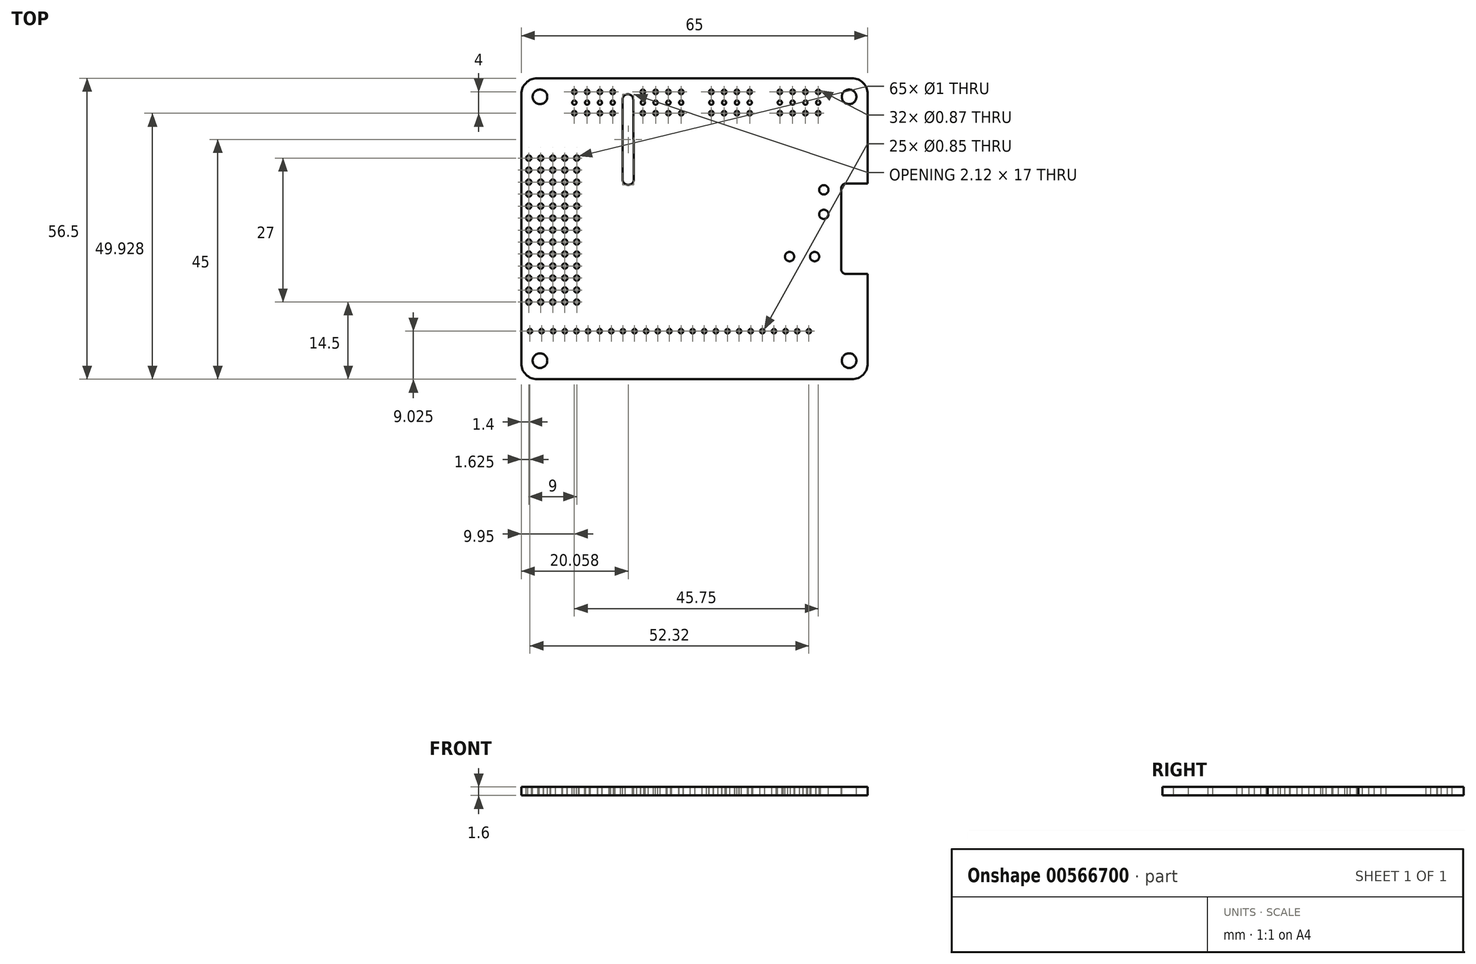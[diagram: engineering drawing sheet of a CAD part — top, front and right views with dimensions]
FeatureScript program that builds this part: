
annotation { "Feature Type Name" : "Feature", "Feature Type Description" : "" }
export const myFeature = defineFeature(function(context is Context, id is Id, definition is map)
    precondition{}
    {
        {
            var Q0;
            Q0=qCreatedBy(makeId("Top.planeOp"),FACE);
            var sketch = newSketch(context, id + "F0", { "sketchPlane" : qUnion([Q0])});
            skLineSegment(sketch, "E0.bottom", {"start": v(32.5, 28.25) * mm, "end": v(-32.5, 28.25) * mm});
            skLineSegment(sketch, "E0.top", {"start": v(32.5, -28.25) * mm, "end": v(-32.5, -28.25) * mm});
            skLineSegment(sketch, "E0.left", {"start": v(32.5, 28.25) * mm, "end": v(32.5, -28.25) * mm});
            skLineSegment(sketch, "E0.right", {"start": v(-32.5, 28.25) * mm, "end": v(-32.5, -28.25) * mm});
            skPoint(sketch, "E0.middle", {"position": v(0, 0) * mm});
            skSolve(sketch);
        }
        {
            var Q0;
            Q0=makeQuery(id+"F0.imprint","IMPRINT",FACE,{"disambiguationData":[TD([[makeQuery(id+"F0.imprint","IMPRINT",EDGE,{"derivedFrom":sQuery(id+"F0.wireOp",EDGE,"E0.bottom")}),1.0]])]});
            extrude(context, id + "F1", {"entities" : qUnion([Q0]), "depth" : 1.6 * mm, "offsetDistance" : 25 * mm});
        }
        {
            var Q0;
            Q0=makeQuery(id+"F1.opExtrude","SWEPT_EDGE",EDGE,{"disambiguationData":[OSD([sQuery(id+"F0.wireOp",EDGE,"E0.top"),sQuery(id+"F0.wireOp",EDGE,"E0.right")])]});
            var Q1;
            Q1=makeQuery(id+"F1.opExtrude","SWEPT_EDGE",EDGE,{"disambiguationData":[OSD([sQuery(id+"F0.wireOp",EDGE,"E0.top"),sQuery(id+"F0.wireOp",EDGE,"E0.left")])]});
            var Q2;
            Q2=makeQuery(id+"F1.opExtrude","SWEPT_EDGE",EDGE,{"disambiguationData":[OSD([sQuery(id+"F0.wireOp",EDGE,"E0.bottom"),sQuery(id+"F0.wireOp",EDGE,"E0.left")])]});
            var Q3;
            Q3=makeQuery(id+"F1.opExtrude","SWEPT_EDGE",EDGE,{"disambiguationData":[OSD([sQuery(id+"F0.wireOp",EDGE,"E0.bottom"),sQuery(id+"F0.wireOp",EDGE,"E0.right")])]});
            fillet(context, id + "F2", {"entities" : qUnion([Q0, Q1, Q2, Q3]), "radius" : 3 * mm, "tangentPropagation" : true, "allowEdgeOverflow" : false});
        }
        {
            var Q0;
            Q0=makeQuery(id+"F1.opExtrude","CAP_FACE",FACE,{"disambiguationData":[OSD([sQuery(id+"F0.wireOp",EDGE,"E0.bottom"),sQuery(id+"F0.wireOp",EDGE,"E0.top"),sQuery(id+"F0.wireOp",EDGE,"E0.left"),sQuery(id+"F0.wireOp",EDGE,"E0.right")])],"isStart":false});
            var sketch = newSketch(context, id + "F3", { "sketchPlane" : qUnion([Q0])});
            skLineSegment(sketch, "E1.bottom", {"start": v(32.5, -8.5) * mm, "end": v(27.5, -8.5) * mm});
            skLineSegment(sketch, "E1.top", {"start": v(32.5, 8.5) * mm, "end": v(27.5, 8.5) * mm});
            skLineSegment(sketch, "E1.left", {"start": v(32.5, -8.5) * mm, "end": v(32.5, 8.5) * mm});
            skLineSegment(sketch, "E1.right", {"start": v(27.5, -8.5) * mm, "end": v(27.5, 8.5) * mm});
            skLineSegment(sketch, "E2", {"start": v(0, 0) * mm, "end": v(36, 0) * mm, "construction": true});
            skSolve(sketch);
        }
        {
            var Q0;
            Q0=makeQuery(id+"F3.imprint","IMPRINT",FACE,{"disambiguationData":[TD([[makeQuery(id+"F3.imprint","IMPRINT",EDGE,{"derivedFrom":sQuery(id+"F3.wireOp",EDGE,"E1.bottom")}),-1.0]])]});
            extrude(context, id + "F4", {"entities" : qUnion([Q0]), "operationType" : NewBodyOperationType.REMOVE, "endBound" : BoundingType.THROUGH_ALL, "oppositeDirection" : true, "depth" : 25 * mm, "offsetDistance" : 25 * mm});
        }
        {
            var Q0;
            Q0=makeQuery(id+"F4.boolean.opBoolean","COPY",EDGE,{"derivedFrom":makeQuery(id+"F4.opExtrude","SWEPT_EDGE",EDGE,{"disambiguationData":[OSD([sQuery(id+"F3.wireOp",EDGE,"E1.bottom"),sQuery(id+"F3.wireOp",EDGE,"E1.right")])]})});
            var Q1;
            Q1=makeQuery(id+"F4.boolean.opBoolean","COPY",EDGE,{"derivedFrom":makeQuery(id+"F4.opExtrude","SWEPT_EDGE",EDGE,{"disambiguationData":[OSD([sQuery(id+"F3.wireOp",EDGE,"E1.top"),sQuery(id+"F3.wireOp",EDGE,"E1.right")])]})});
            fillet(context, id + "F5", {"entities" : qUnion([Q0, Q1]), "radius" : 1 * mm, "tangentPropagation" : true, "allowEdgeOverflow" : false});
        }
        {
            var Q0;
            Q0=makeQuery(id+"F1.opExtrude","CAP_FACE",FACE,{"disambiguationData":[OSD([sQuery(id+"F0.wireOp",EDGE,"E0.bottom"),sQuery(id+"F0.wireOp",EDGE,"E0.top"),sQuery(id+"F0.wireOp",EDGE,"E0.left"),sQuery(id+"F0.wireOp",EDGE,"E0.right")])],"isStart":false});
            var sketch = newSketch(context, id + "F6", { "sketchPlane" : qUnion([Q0])});
            skCircle(sketch, "E3", {"center": v(-29, -24.75) * mm, "radius": 1.38 * mm});
            skCircle(sketch, "E4.MirrorC", {"center": v(29, -24.75) * mm, "radius": 1.38 * mm});
            skCircle(sketch, "E5.MirrorC", {"center": v(-29, 24.75) * mm, "radius": 1.38 * mm});
            skCircle(sketch, "E6.MirrorC", {"center": v(29, 24.75) * mm, "radius": 1.38 * mm});
            skSolve(sketch);
        }
        {
            var Q0;
            Q0 = qSketchRegion(id + "F6", true);
            extrude(context, id + "F7", {"entities" : qUnion([Q0]), "operationType" : NewBodyOperationType.REMOVE, "endBound" : BoundingType.THROUGH_ALL, "oppositeDirection" : true, "depth" : 25 * mm, "offsetDistance" : 25 * mm});
        }
        {
            var Q0;
            Q0=makeQuery(id+"F1.opExtrude","CAP_FACE",FACE,{"disambiguationData":[OSD([sQuery(id+"F0.wireOp",EDGE,"E0.bottom"),sQuery(id+"F0.wireOp",EDGE,"E0.top"),sQuery(id+"F0.wireOp",EDGE,"E0.left"),sQuery(id+"F0.wireOp",EDGE,"E0.right")])],"isStart":false});
            var sketch = newSketch(context, id + "F8", { "sketchPlane" : qUnion([Q0])});
            skCircle(sketch, "E7", {"center": v(-31.1, -13.75) * mm, "radius": 0.5 * mm});
            skCircle(sketch, "E8.0.1.0", {"center": v(-31.1, -11.5) * mm, "radius": 0.5 * mm});
            skCircle(sketch, "E8.0.2.0", {"center": v(-31.1, -9.25) * mm, "radius": 0.5 * mm});
            skCircle(sketch, "E8.0.3.0", {"center": v(-31.1, -7) * mm, "radius": 0.5 * mm});
            skCircle(sketch, "E8.0.4.0", {"center": v(-31.1, -4.75) * mm, "radius": 0.5 * mm});
            skCircle(sketch, "E8.0.5.0", {"center": v(-31.1, -2.5) * mm, "radius": 0.5 * mm});
            skCircle(sketch, "E8.0.6.0", {"center": v(-31.1, -0.25) * mm, "radius": 0.5 * mm});
            skCircle(sketch, "E8.0.7.0", {"center": v(-31.1, 2) * mm, "radius": 0.5 * mm});
            skCircle(sketch, "E8.0.8.0", {"center": v(-31.1, 4.25) * mm, "radius": 0.5 * mm});
            skCircle(sketch, "E8.0.9.0", {"center": v(-31.1, 6.5) * mm, "radius": 0.5 * mm});
            skCircle(sketch, "E8.0.10.0", {"center": v(-31.1, 8.75) * mm, "radius": 0.5 * mm});
            skCircle(sketch, "E8.0.11.0", {"center": v(-31.1, 11) * mm, "radius": 0.5 * mm});
            skCircle(sketch, "E8.0.12.0", {"center": v(-31.1, 13.25) * mm, "radius": 0.5 * mm});
            skCircle(sketch, "E8.1.0.0", {"center": v(-28.85, -13.75) * mm, "radius": 0.5 * mm});
            skCircle(sketch, "E8.1.1.0", {"center": v(-28.85, -11.5) * mm, "radius": 0.5 * mm});
            skCircle(sketch, "E8.1.2.0", {"center": v(-28.85, -9.25) * mm, "radius": 0.5 * mm});
            skCircle(sketch, "E8.1.3.0", {"center": v(-28.85, -7) * mm, "radius": 0.5 * mm});
            skCircle(sketch, "E8.1.4.0", {"center": v(-28.85, -4.75) * mm, "radius": 0.5 * mm});
            skCircle(sketch, "E8.1.5.0", {"center": v(-28.85, -2.5) * mm, "radius": 0.5 * mm});
            skCircle(sketch, "E8.1.6.0", {"center": v(-28.85, -0.25) * mm, "radius": 0.5 * mm});
            skCircle(sketch, "E8.1.7.0", {"center": v(-28.85, 2) * mm, "radius": 0.5 * mm});
            skCircle(sketch, "E8.1.8.0", {"center": v(-28.85, 4.25) * mm, "radius": 0.5 * mm});
            skCircle(sketch, "E8.1.9.0", {"center": v(-28.85, 6.5) * mm, "radius": 0.5 * mm});
            skCircle(sketch, "E8.1.10.0", {"center": v(-28.85, 8.75) * mm, "radius": 0.5 * mm});
            skCircle(sketch, "E8.1.11.0", {"center": v(-28.85, 11) * mm, "radius": 0.5 * mm});
            skCircle(sketch, "E8.1.12.0", {"center": v(-28.85, 13.25) * mm, "radius": 0.5 * mm});
            skCircle(sketch, "E8.2.0.0", {"center": v(-26.6, -13.75) * mm, "radius": 0.5 * mm});
            skCircle(sketch, "E8.2.1.0", {"center": v(-26.6, -11.5) * mm, "radius": 0.5 * mm});
            skCircle(sketch, "E8.2.2.0", {"center": v(-26.6, -9.25) * mm, "radius": 0.5 * mm});
            skCircle(sketch, "E8.2.3.0", {"center": v(-26.6, -7) * mm, "radius": 0.5 * mm});
            skCircle(sketch, "E8.2.4.0", {"center": v(-26.6, -4.75) * mm, "radius": 0.5 * mm});
            skCircle(sketch, "E8.2.5.0", {"center": v(-26.6, -2.5) * mm, "radius": 0.5 * mm});
            skCircle(sketch, "E8.2.6.0", {"center": v(-26.6, -0.25) * mm, "radius": 0.5 * mm});
            skCircle(sketch, "E8.2.7.0", {"center": v(-26.6, 2) * mm, "radius": 0.5 * mm});
            skCircle(sketch, "E8.2.8.0", {"center": v(-26.6, 4.25) * mm, "radius": 0.5 * mm});
            skCircle(sketch, "E8.2.9.0", {"center": v(-26.6, 6.5) * mm, "radius": 0.5 * mm});
            skCircle(sketch, "E8.2.10.0", {"center": v(-26.6, 8.75) * mm, "radius": 0.5 * mm});
            skCircle(sketch, "E8.2.11.0", {"center": v(-26.6, 11) * mm, "radius": 0.5 * mm});
            skCircle(sketch, "E8.2.12.0", {"center": v(-26.6, 13.25) * mm, "radius": 0.5 * mm});
            skCircle(sketch, "E8.3.0.0", {"center": v(-24.35, -13.75) * mm, "radius": 0.5 * mm});
            skCircle(sketch, "E8.3.1.0", {"center": v(-24.35, -11.5) * mm, "radius": 0.5 * mm});
            skCircle(sketch, "E8.3.2.0", {"center": v(-24.35, -9.25) * mm, "radius": 0.5 * mm});
            skCircle(sketch, "E8.3.3.0", {"center": v(-24.35, -7) * mm, "radius": 0.5 * mm});
            skCircle(sketch, "E8.3.4.0", {"center": v(-24.35, -4.75) * mm, "radius": 0.5 * mm});
            skCircle(sketch, "E8.3.5.0", {"center": v(-24.35, -2.5) * mm, "radius": 0.5 * mm});
            skCircle(sketch, "E8.3.6.0", {"center": v(-24.35, -0.25) * mm, "radius": 0.5 * mm});
            skCircle(sketch, "E8.3.7.0", {"center": v(-24.35, 2) * mm, "radius": 0.5 * mm});
            skCircle(sketch, "E8.3.8.0", {"center": v(-24.35, 4.25) * mm, "radius": 0.5 * mm});
            skCircle(sketch, "E8.3.9.0", {"center": v(-24.35, 6.5) * mm, "radius": 0.5 * mm});
            skCircle(sketch, "E8.3.10.0", {"center": v(-24.35, 8.75) * mm, "radius": 0.5 * mm});
            skCircle(sketch, "E8.3.11.0", {"center": v(-24.35, 11) * mm, "radius": 0.5 * mm});
            skCircle(sketch, "E8.3.12.0", {"center": v(-24.35, 13.25) * mm, "radius": 0.5 * mm});
            skCircle(sketch, "E8.4.0.0", {"center": v(-22.1, -13.75) * mm, "radius": 0.5 * mm});
            skCircle(sketch, "E8.4.1.0", {"center": v(-22.1, -11.5) * mm, "radius": 0.5 * mm});
            skCircle(sketch, "E8.4.2.0", {"center": v(-22.1, -9.25) * mm, "radius": 0.5 * mm});
            skCircle(sketch, "E8.4.3.0", {"center": v(-22.1, -7) * mm, "radius": 0.5 * mm});
            skCircle(sketch, "E8.4.4.0", {"center": v(-22.1, -4.75) * mm, "radius": 0.5 * mm});
            skCircle(sketch, "E8.4.5.0", {"center": v(-22.1, -2.5) * mm, "radius": 0.5 * mm});
            skCircle(sketch, "E8.4.6.0", {"center": v(-22.1, -0.25) * mm, "radius": 0.5 * mm});
            skCircle(sketch, "E8.4.7.0", {"center": v(-22.1, 2) * mm, "radius": 0.5 * mm});
            skCircle(sketch, "E8.4.8.0", {"center": v(-22.1, 4.25) * mm, "radius": 0.5 * mm});
            skCircle(sketch, "E8.4.9.0", {"center": v(-22.1, 6.5) * mm, "radius": 0.5 * mm});
            skCircle(sketch, "E8.4.10.0", {"center": v(-22.1, 8.75) * mm, "radius": 0.5 * mm});
            skCircle(sketch, "E8.4.11.0", {"center": v(-22.1, 11) * mm, "radius": 0.5 * mm});
            skCircle(sketch, "E8.4.12.0", {"center": v(-22.1, 13.25) * mm, "radius": 0.5 * mm});
            skLineSegment(sketch, "E8.direction1", {"start": v(-31.2, -13.8) * mm, "end": v(-28.95, -13.8) * mm, "construction": true});
            skLineSegment(sketch, "E8.direction2", {"start": v(-31.2, -13.8) * mm, "end": v(-31.2, 11.2) * mm, "construction": true});
            skCircle(sketch, "E9", {"center": v(-30.87, -19.23) * mm, "radius": 0.42 * mm});
            skCircle(sketch, "E10.1.0.0", {"center": v(-28.7, -19.23) * mm, "radius": 0.42 * mm});
            skCircle(sketch, "E10.2.0.0", {"center": v(-26.51, -19.23) * mm, "radius": 0.42 * mm});
            skCircle(sketch, "E10.3.0.0", {"center": v(-24.33, -19.23) * mm, "radius": 0.42 * mm});
            skCircle(sketch, "E10.4.0.0", {"center": v(-22.15, -19.23) * mm, "radius": 0.42 * mm});
            skCircle(sketch, "E10.5.0.0", {"center": v(-19.97, -19.23) * mm, "radius": 0.42 * mm});
            skCircle(sketch, "E10.6.0.0", {"center": v(-17.8, -19.23) * mm, "radius": 0.42 * mm});
            skCircle(sketch, "E10.7.0.0", {"center": v(-15.61, -19.23) * mm, "radius": 0.42 * mm});
            skCircle(sketch, "E10.8.0.0", {"center": v(-13.43, -19.23) * mm, "radius": 0.42 * mm});
            skCircle(sketch, "E10.9.0.0", {"center": v(-11.25, -19.23) * mm, "radius": 0.42 * mm});
            skCircle(sketch, "E10.10.0.0", {"center": v(-9.07, -19.23) * mm, "radius": 0.42 * mm});
            skCircle(sketch, "E10.11.0.0", {"center": v(-6.9, -19.23) * mm, "radius": 0.42 * mm});
            skCircle(sketch, "E10.12.0.0", {"center": v(-4.71, -19.23) * mm, "radius": 0.42 * mm});
            skCircle(sketch, "E10.13.0.0", {"center": v(-2.53, -19.23) * mm, "radius": 0.42 * mm});
            skCircle(sketch, "E10.14.0.0", {"center": v(-0.35, -19.23) * mm, "radius": 0.42 * mm});
            skCircle(sketch, "E10.15.0.0", {"center": v(1.83, -19.23) * mm, "radius": 0.42 * mm});
            skCircle(sketch, "E10.16.0.0", {"center": v(4, -19.23) * mm, "radius": 0.42 * mm});
            skCircle(sketch, "E10.17.0.0", {"center": v(6.19, -19.23) * mm, "radius": 0.42 * mm});
            skCircle(sketch, "E10.18.0.0", {"center": v(8.37, -19.23) * mm, "radius": 0.42 * mm});
            skCircle(sketch, "E10.19.0.0", {"center": v(10.55, -19.23) * mm, "radius": 0.42 * mm});
            skCircle(sketch, "E10.20.0.0", {"center": v(12.73, -19.23) * mm, "radius": 0.42 * mm});
            skCircle(sketch, "E10.21.0.0", {"center": v(14.9, -19.23) * mm, "radius": 0.42 * mm});
            skCircle(sketch, "E10.22.0.0", {"center": v(17.09, -19.23) * mm, "radius": 0.42 * mm});
            skCircle(sketch, "E10.23.0.0", {"center": v(19.27, -19.23) * mm, "radius": 0.42 * mm});
            skCircle(sketch, "E10.24.0.0", {"center": v(21.45, -19.23) * mm, "radius": 0.42 * mm});
            skLineSegment(sketch, "E10.direction1", {"start": v(-30.87, -19.23) * mm, "end": v(-28.7, -19.23) * mm, "construction": true});
            skSolve(sketch);
        }
        {
            var Q0;
            Q0 = qSketchRegion(id + "F8", true);
            extrude(context, id + "F9", {"entities" : qUnion([Q0]), "operationType" : NewBodyOperationType.REMOVE, "endBound" : BoundingType.THROUGH_ALL, "oppositeDirection" : true, "depth" : 25 * mm, "offsetDistance" : 25 * mm});
        }
        {
            var Q0;
            Q0=makeQuery(id+"F1.opExtrude","CAP_FACE",FACE,{"disambiguationData":[OSD([sQuery(id+"F0.wireOp",EDGE,"E0.bottom"),sQuery(id+"F0.wireOp",EDGE,"E0.top"),sQuery(id+"F0.wireOp",EDGE,"E0.left"),sQuery(id+"F0.wireOp",EDGE,"E0.right")])],"isStart":false});
            var sketch = newSketch(context, id + "F10", { "sketchPlane" : qUnion([Q0])});
            skLineSegment(sketch, "E11.MirrorCS", {"start": v(-13.5, 8.25) * mm, "end": v(-11.38, 8.25) * mm});
            skLineSegment(sketch, "E12.MirrorCS", {"start": v(-13.5, 25.25) * mm, "end": v(-11.5, 25.25) * mm});
            skLineSegment(sketch, "E13.MirrorCS", {"start": v(-13.5, 25.25) * mm, "end": v(-13.5, 8.25) * mm});
            skLineSegment(sketch, "E14.MirrorCS", {"start": v(-11.5, 25.25) * mm, "end": v(-11.38, 8.25) * mm});
            skLineSegment(sketch, "E15", {"start": v(-13.5, 16.75) * mm, "end": v(-11.44, 16.75) * mm, "construction": true});
            skLineSegment(sketch, "E16", {"start": v(-12.5, 25.25) * mm, "end": v(-12.5, 8.25) * mm, "construction": true});
            skSolve(sketch);
        }
        {
            var Q0;
            Q0 = qSketchRegion(id + "F10", true);
            extrude(context, id + "F11", {"entities" : qUnion([Q0]), "operationType" : NewBodyOperationType.REMOVE, "endBound" : BoundingType.THROUGH_ALL, "oppositeDirection" : true, "depth" : 25 * mm, "offsetDistance" : 25 * mm});
        }
        {
            var Q0;
            Q0=makeQuery(id+"F11.boolean.opBoolean","COPY",EDGE,{"derivedFrom":makeQuery(id+"F11.opExtrude","SWEPT_EDGE",EDGE,{"disambiguationData":[OSD([sQuery(id+"F10.wireOp",EDGE,"E11.MirrorCS"),sQuery(id+"F10.wireOp",EDGE,"E14.MirrorCS")])]})});
            var Q1;
            Q1=makeQuery(id+"F11.boolean.opBoolean","COPY",EDGE,{"derivedFrom":makeQuery(id+"F11.opExtrude","SWEPT_EDGE",EDGE,{"disambiguationData":[OSD([sQuery(id+"F10.wireOp",EDGE,"E11.MirrorCS"),sQuery(id+"F10.wireOp",EDGE,"E13.MirrorCS")])]})});
            var Q2;
            Q2=makeQuery(id+"F11.boolean.opBoolean","COPY",EDGE,{"derivedFrom":makeQuery(id+"F11.opExtrude","SWEPT_EDGE",EDGE,{"disambiguationData":[OSD([sQuery(id+"F10.wireOp",EDGE,"E12.MirrorCS"),sQuery(id+"F10.wireOp",EDGE,"E13.MirrorCS")])]})});
            var Q3;
            Q3=makeQuery(id+"F11.boolean.opBoolean","COPY",EDGE,{"derivedFrom":makeQuery(id+"F11.opExtrude","SWEPT_EDGE",EDGE,{"disambiguationData":[OSD([sQuery(id+"F10.wireOp",EDGE,"E12.MirrorCS"),sQuery(id+"F10.wireOp",EDGE,"E14.MirrorCS")])]})});
            fillet(context, id + "F12", {"entities" : qUnion([Q0, Q1, Q2, Q3]), "radius" : 1 * mm, "tangentPropagation" : true, "allowEdgeOverflow" : false});
        }
        {
            var Q0;
            Q0=makeQuery(id+"F1.opExtrude","CAP_FACE",FACE,{"disambiguationData":[OSD([sQuery(id+"F0.wireOp",EDGE,"E0.bottom"),sQuery(id+"F0.wireOp",EDGE,"E0.top"),sQuery(id+"F0.wireOp",EDGE,"E0.left"),sQuery(id+"F0.wireOp",EDGE,"E0.right")])],"isStart":false});
            var sketch = newSketch(context, id + "F13", { "sketchPlane" : qUnion([Q0])});
            skCircle(sketch, "E17", {"center": v(22.52, -5.23) * mm, "radius": 0.88 * mm});
            skCircle(sketch, "E18", {"center": v(17.82, -5.23) * mm, "radius": 0.88 * mm});
            skCircle(sketch, "E19", {"center": v(24.25, 2.7) * mm, "radius": 0.88 * mm});
            skCircle(sketch, "E20", {"center": v(24.25, 7.3) * mm, "radius": 0.88 * mm});
            skSolve(sketch);
        }
        {
            var Q0;
            Q0=makeQuery(id+"F13.imprint","IMPRINT",FACE,{"disambiguationData":[TD([[makeQuery(id+"F13.imprint","IMPRINT",EDGE,{"derivedFrom":sQuery(id+"F13.wireOp",EDGE,"E18")}),1.0]])]});
            var Q1;
            Q1=makeQuery(id+"F13.imprint","IMPRINT",FACE,{"disambiguationData":[TD([[makeQuery(id+"F13.imprint","IMPRINT",EDGE,{"derivedFrom":sQuery(id+"F13.wireOp",EDGE,"E17")}),1.0]])]});
            var Q2;
            Q2=makeQuery(id+"F13.imprint","IMPRINT",FACE,{"disambiguationData":[TD([[makeQuery(id+"F13.imprint","IMPRINT",EDGE,{"derivedFrom":sQuery(id+"F13.wireOp",EDGE,"E19")}),1.0]])]});
            var Q3;
            Q3=makeQuery(id+"F13.imprint","IMPRINT",FACE,{"disambiguationData":[TD([[makeQuery(id+"F13.imprint","IMPRINT",EDGE,{"derivedFrom":sQuery(id+"F13.wireOp",EDGE,"E20")}),1.0]])]});
            extrude(context, id + "F14", {"entities" : qUnion([Q0, Q1, Q2, Q3]), "operationType" : NewBodyOperationType.REMOVE, "endBound" : BoundingType.THROUGH_ALL, "oppositeDirection" : true, "depth" : 25 * mm, "offsetDistance" : 25 * mm});
        }
        {
            var Q0;
            Q0=makeQuery(id+"F1.opExtrude","CAP_FACE",FACE,{"disambiguationData":[OSD([sQuery(id+"F0.wireOp",EDGE,"E0.bottom"),sQuery(id+"F0.wireOp",EDGE,"E0.top"),sQuery(id+"F0.wireOp",EDGE,"E0.left"),sQuery(id+"F0.wireOp",EDGE,"E0.right")])],"isStart":false});
            var sketch = newSketch(context, id + "F15", { "sketchPlane" : qUnion([Q0])});
            skCircle(sketch, "E21", {"center": v(23.2, 25.68) * mm, "radius": 0.43 * mm});
            skCircle(sketch, "E22", {"center": v(23.2, 23.68) * mm, "radius": 0.4 * mm});
            skCircle(sketch, "E23", {"center": v(23.2, 21.68) * mm, "radius": 0.43 * mm});
            skCircle(sketch, "E24.1.0.0", {"center": v(20.8, 21.68) * mm, "radius": 0.43 * mm});
            skCircle(sketch, "E24.1.0.1", {"center": v(20.8, 23.68) * mm, "radius": 0.4 * mm});
            skCircle(sketch, "E24.1.0.2", {"center": v(20.8, 25.68) * mm, "radius": 0.43 * mm});
            skCircle(sketch, "E24.2.0.0", {"center": v(18.4, 21.68) * mm, "radius": 0.43 * mm});
            skCircle(sketch, "E24.2.0.1", {"center": v(18.4, 23.68) * mm, "radius": 0.4 * mm});
            skCircle(sketch, "E24.2.0.2", {"center": v(18.4, 25.68) * mm, "radius": 0.43 * mm});
            skCircle(sketch, "E24.3.0.0", {"center": v(16, 21.68) * mm, "radius": 0.43 * mm});
            skCircle(sketch, "E24.3.0.1", {"center": v(16, 23.68) * mm, "radius": 0.4 * mm});
            skCircle(sketch, "E24.3.0.2", {"center": v(16, 25.68) * mm, "radius": 0.43 * mm});
            skLineSegment(sketch, "E24.direction1", {"start": v(23.2, 21.68) * mm, "end": v(20.8, 21.68) * mm, "construction": true});
            skLineSegment(sketch, "E25.1.0.0", {"start": v(10.35, 21.68) * mm, "end": v(7.95, 21.68) * mm, "construction": true});
            skCircle(sketch, "E25.1.0.1", {"center": v(3.15, 25.68) * mm, "radius": 0.43 * mm});
            skCircle(sketch, "E25.1.0.2", {"center": v(3.15, 23.68) * mm, "radius": 0.4 * mm});
            skCircle(sketch, "E25.1.0.3", {"center": v(3.15, 21.68) * mm, "radius": 0.43 * mm});
            skCircle(sketch, "E25.1.0.4", {"center": v(5.55, 25.68) * mm, "radius": 0.43 * mm});
            skCircle(sketch, "E25.1.0.5", {"center": v(5.55, 23.68) * mm, "radius": 0.4 * mm});
            skCircle(sketch, "E25.1.0.6", {"center": v(5.55, 21.68) * mm, "radius": 0.43 * mm});
            skCircle(sketch, "E25.1.0.7", {"center": v(7.95, 25.68) * mm, "radius": 0.43 * mm});
            skCircle(sketch, "E25.1.0.8", {"center": v(7.95, 23.68) * mm, "radius": 0.4 * mm});
            skCircle(sketch, "E25.1.0.9", {"center": v(7.95, 21.68) * mm, "radius": 0.43 * mm});
            skCircle(sketch, "E25.1.0.10", {"center": v(10.35, 21.68) * mm, "radius": 0.43 * mm});
            skCircle(sketch, "E25.1.0.11", {"center": v(10.35, 23.68) * mm, "radius": 0.4 * mm});
            skCircle(sketch, "E25.1.0.12", {"center": v(10.35, 25.68) * mm, "radius": 0.43 * mm});
            skLineSegment(sketch, "E25.2.0.0", {"start": v(-2.5, 21.68) * mm, "end": v(-4.9, 21.68) * mm, "construction": true});
            skCircle(sketch, "E25.2.0.1", {"center": v(-9.7, 25.68) * mm, "radius": 0.43 * mm});
            skCircle(sketch, "E25.2.0.2", {"center": v(-9.7, 23.68) * mm, "radius": 0.4 * mm});
            skCircle(sketch, "E25.2.0.3", {"center": v(-9.7, 21.68) * mm, "radius": 0.43 * mm});
            skCircle(sketch, "E25.2.0.4", {"center": v(-7.3, 25.68) * mm, "radius": 0.43 * mm});
            skCircle(sketch, "E25.2.0.5", {"center": v(-7.3, 23.68) * mm, "radius": 0.4 * mm});
            skCircle(sketch, "E25.2.0.6", {"center": v(-7.3, 21.68) * mm, "radius": 0.43 * mm});
            skCircle(sketch, "E25.2.0.7", {"center": v(-4.9, 25.68) * mm, "radius": 0.43 * mm});
            skCircle(sketch, "E25.2.0.8", {"center": v(-4.9, 23.68) * mm, "radius": 0.4 * mm});
            skCircle(sketch, "E25.2.0.9", {"center": v(-4.9, 21.68) * mm, "radius": 0.43 * mm});
            skCircle(sketch, "E25.2.0.10", {"center": v(-2.5, 21.68) * mm, "radius": 0.43 * mm});
            skCircle(sketch, "E25.2.0.11", {"center": v(-2.5, 23.68) * mm, "radius": 0.4 * mm});
            skCircle(sketch, "E25.2.0.12", {"center": v(-2.5, 25.68) * mm, "radius": 0.43 * mm});
            skLineSegment(sketch, "E25.3.0.0", {"start": v(-15.35, 21.68) * mm, "end": v(-17.75, 21.68) * mm, "construction": true});
            skCircle(sketch, "E25.3.0.1", {"center": v(-22.55, 25.68) * mm, "radius": 0.43 * mm});
            skCircle(sketch, "E25.3.0.2", {"center": v(-22.55, 23.68) * mm, "radius": 0.4 * mm});
            skCircle(sketch, "E25.3.0.3", {"center": v(-22.55, 21.68) * mm, "radius": 0.43 * mm});
            skCircle(sketch, "E25.3.0.4", {"center": v(-20.15, 25.68) * mm, "radius": 0.43 * mm});
            skCircle(sketch, "E25.3.0.5", {"center": v(-20.15, 23.68) * mm, "radius": 0.4 * mm});
            skCircle(sketch, "E25.3.0.6", {"center": v(-20.15, 21.68) * mm, "radius": 0.43 * mm});
            skCircle(sketch, "E25.3.0.7", {"center": v(-17.75, 25.68) * mm, "radius": 0.43 * mm});
            skCircle(sketch, "E25.3.0.8", {"center": v(-17.75, 23.68) * mm, "radius": 0.4 * mm});
            skCircle(sketch, "E25.3.0.9", {"center": v(-17.75, 21.68) * mm, "radius": 0.43 * mm});
            skCircle(sketch, "E25.3.0.10", {"center": v(-15.35, 21.68) * mm, "radius": 0.43 * mm});
            skCircle(sketch, "E25.3.0.11", {"center": v(-15.35, 23.68) * mm, "radius": 0.4 * mm});
            skCircle(sketch, "E25.3.0.12", {"center": v(-15.35, 25.68) * mm, "radius": 0.43 * mm});
            skLineSegment(sketch, "E25.direction1", {"start": v(16, 21.68) * mm, "end": v(3.15, 21.68) * mm, "construction": true});
            skSolve(sketch);
        }
        {
            var Q0;
            Q0 = qSketchRegion(id + "F15", true);
            extrude(context, id + "F16", {"entities" : qUnion([Q0]), "operationType" : NewBodyOperationType.REMOVE, "endBound" : BoundingType.THROUGH_ALL, "oppositeDirection" : true, "depth" : 25 * mm, "offsetDistance" : 25 * mm});
        }
    });
